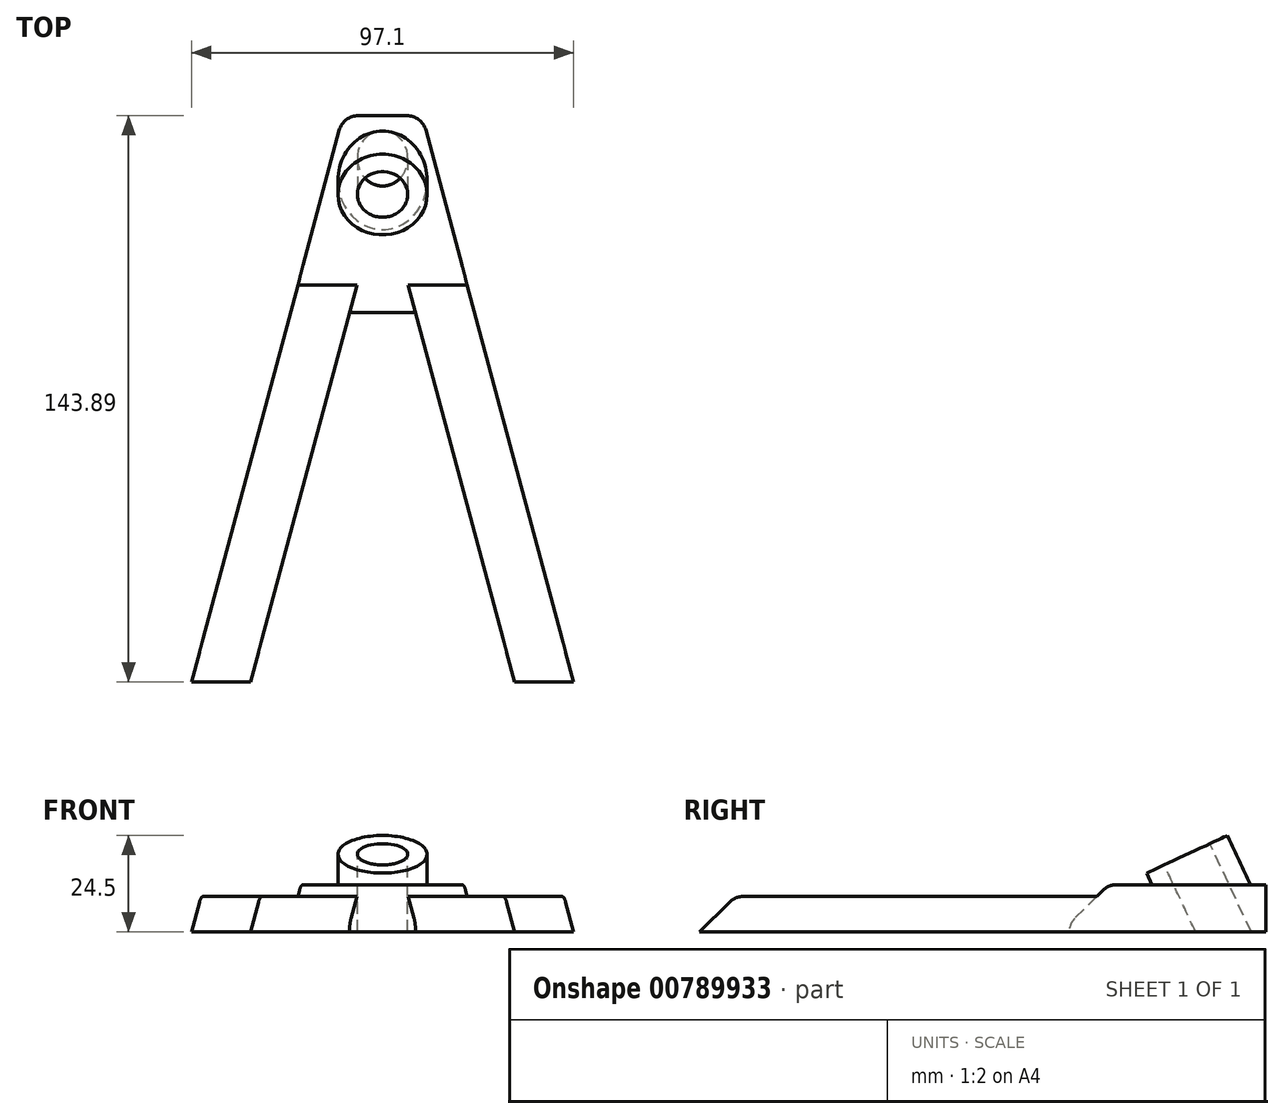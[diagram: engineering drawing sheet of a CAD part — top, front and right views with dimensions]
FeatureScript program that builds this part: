
annotation { "Feature Type Name" : "Feature", "Feature Type Description" : "" }
export const myFeature = defineFeature(function(context is Context, id is Id, definition is map)
    precondition{}
    {
        {
            var Q0;
            Q0=qCreatedBy(makeId("Top.planeOp"),FACE);
            var sketch = newSketch(context, id + "F0", { "sketchPlane" : qUnion([Q0])});
            skLineSegment(sketch, "E0", {"start": v(-48.82, -144.89) * mm, "end": v(-10, 0) * mm});
            skLineSegment(sketch, "E1", {"start": v(10, 0) * mm, "end": v(48.82, -144.89) * mm});
            skLineSegment(sketch, "E2", {"start": v(-48.82, -144.89) * mm, "end": v(-33.82, -144.89) * mm});
            skLineSegment(sketch, "E3", {"start": v(33.82, -144.89) * mm, "end": v(48.82, -144.89) * mm});
            skLineSegment(sketch, "E4", {"start": v(-33.82, -144.89) * mm, "end": v(-8.4, -50) * mm});
            skLineSegment(sketch, "E5", {"start": v(-8.4, -50) * mm, "end": v(8.4, -50) * mm});
            skLineSegment(sketch, "E6", {"start": v(8.4, -50) * mm, "end": v(33.82, -144.89) * mm});
            skPoint(sketch, "E7", {"position": v(0, 0) * mm});
            skLineSegment(sketch, "E8", {"start": v(-10, 0) * mm, "end": v(0, 0) * mm});
            skLineSegment(sketch, "E9", {"start": v(10, 0) * mm, "end": v(0, 0) * mm});
            skLineSegment(sketch, "E10", {"start": v(-8.4, -50) * mm, "end": v(-23.4, -50) * mm});
            skLineSegment(sketch, "E11", {"start": v(8.4, -50) * mm, "end": v(23.4, -50) * mm});
            skSolve(sketch);
        }
        {
            var Q0;
            {var subQ0=sQuery(id+"F0.wireOp",EDGE,"E2");Q0=makeQuery(id+"F0.imprint","IMPRINT",FACE,{"disambiguationData":[TD([[makeQuery(id+"F0.imprint","IMPRINT",EDGE,{"derivedFrom":subQ0}),1.0]])]});}
            var Q1;
            {var subQ0=sQuery(id+"F0.wireOp",EDGE,"E3");Q1=makeQuery(id+"F0.imprint","IMPRINT",FACE,{"disambiguationData":[TD([[makeQuery(id+"F0.imprint","IMPRINT",EDGE,{"derivedFrom":subQ0}),1.0]])]});}
            var Q2;
            {var subQ1=sQuery(id+"F0.wireOp",EDGE,"H4eSQYHw-7cAD-bKFQ-VINS-Qkt0nnbU60AQ");Q2=makeQuery(id+"F0.imprint","IMPRINT",FACE,{"disambiguationData":[TD([[makeQuery(id+"F0.imprint","IMPRINT",EDGE,{"derivedFrom":subQ1}),-1.0]])]});}
            var Q3;
            Q3=makeQuery(id+"F0.imprint","IMPRINT",FACE,{"disambiguationData":[TD([[makeQuery(id+"F0.imprint","IMPRINT",EDGE,{"derivedFrom":sQuery(id+"F0.wireOp",EDGE,"E5")}),1.0]])]});
            extrude(context, id + "F1", {"entities" : qUnion([Q0, Q1, Q2, Q3]), "depth" : -9 * mm, "offsetDistance" : 25 * mm});
        }
        {
            var Q0;
            Q0=qCreatedBy(makeId("Right.planeOp"),FACE);
            var sketch = newSketch(context, id + "F2", { "sketchPlane" : qUnion([Q0])});
            skLineSegment(sketch, "E12", {"start": v(-15.5, 1) * mm, "end": v(-20.03, 10.71) * mm});
            skLineSegment(sketch, "E13.0", {"start": v(-3, 1) * mm, "end": v(-9.76, 15.5) * mm});
            skLineSegment(sketch, "E14", {"start": v(-20.03, 10.71) * mm, "end": v(-9.76, 15.5) * mm});
            skLineSegment(sketch, "E15", {"start": v(-15.5, 1) * mm, "end": v(-3, 1) * mm});
            skSolve(sketch);
        }
        {
            var Q0;
            {var subQ0=sQuery(id+"F2.wireOp",EDGE,"E13.0");Q0=makeQuery(id+"F2.imprint","IMPRINT",FACE,{"disambiguationData":[TD([[makeQuery(id+"F2.imprint","IMPRINT",EDGE,{"derivedFrom":subQ0}),1.0]])]});}
            var Q1;
            Q1=sQuery(id+"F2.wireOp",EDGE,"E12");
            revolve(context, id + "F3", {"operationType" : NewBodyOperationType.ADD, "surfaceOperationType" : NewSurfaceOperationType.NEW, "entities" : qUnion([Q0]), "axis" : qUnion([Q1]), "revolveType" : RevolveType.FULL});
        }
        {
            var Q0;
            Q0=makeQuery(id+"F0.imprint","IMPRINT",FACE,{"disambiguationData":[TD([[makeQuery(id+"F0.imprint","IMPRINT",EDGE,{"derivedFrom":sQuery(id+"F0.wireOp",EDGE,"E5")}),1.0]])]});
            extrude(context, id + "F4", {"entities" : qUnion([Q0]), "operationType" : NewBodyOperationType.ADD, "depth" : 3 * mm, "offsetDistance" : 25 * mm});
        }
        {
            var Q0;
            {var subQ0=sQuery(id+"F0.wireOp",EDGE,"E8");var subQ1=sQuery(id+"F0.wireOp",EDGE,"E0");Q0=makeQuery(id+"F4.boolean.opBoolean","MERGE",EDGE,{"derivedFrom":[makeQuery(id+"F1.opExtrude","SWEPT_EDGE",EDGE,{"disambiguationData":[OSD([subQ1,subQ0])]}),makeQuery(id+"F4.opExtrude","SWEPT_EDGE",EDGE,{"disambiguationData":[OSD([subQ1,subQ0])]})]});}
            var Q1;
            {var subQ0=sQuery(id+"F0.wireOp",EDGE,"E9");var subQ1=sQuery(id+"F0.wireOp",EDGE,"E1");Q1=makeQuery(id+"F4.boolean.opBoolean","MERGE",EDGE,{"derivedFrom":[makeQuery(id+"F1.opExtrude","SWEPT_EDGE",EDGE,{"disambiguationData":[OSD([subQ1,subQ0])]}),makeQuery(id+"F4.opExtrude","SWEPT_EDGE",EDGE,{"disambiguationData":[OSD([subQ1,subQ0])]})]});}
            fillet(context, id + "F5", {"entities" : qUnion([Q0, Q1]), "radius" : 5 * mm, "tangentPropagation" : true, "allowEdgeOverflow" : false});
        }
        {
            var Q0;
            Q0=makeQuery(id+"F3.opRevolve","SWEPT_FACE",FACE,{"disambiguationData":[OSD([sQuery(id+"F2.wireOp",EDGE,"E14")])]});
            var sketch = newSketch(context, id + "F6", { "sketchPlane" : qUnion([Q0])});
            skCircle(sketch, "E16", {"center": v(0, -13.63) * mm, "radius": 6.4 * mm});
            skSolve(sketch);
        }
        {
            var Q0;
            Q0=makeQuery(id+"F6.imprint","IMPRINT",FACE,{"disambiguationData":[TD([[makeQuery(id+"F6.imprint","IMPRINT",EDGE,{"derivedFrom":sQuery(id+"F6.wireOp",EDGE,"E16")}),1.0]])]});
            extrude(context, id + "F7", {"entities" : qUnion([Q0]), "operationType" : NewBodyOperationType.REMOVE, "oppositeDirection" : true, "depth" : 30 * mm, "offsetDistance" : 25 * mm});
        }
        {
            var Q0;
            Q0=makeQuery(id+"F4.opExtrude","CAP_EDGE",EDGE,{"disambiguationData":[OSD([sQuery(id+"F0.wireOp",EDGE,"E5"),sQuery(id+"F0.wireOp",EDGE,"E10"),sQuery(id+"F0.wireOp",EDGE,"E11")])],"isStart":false});
            var Q1;
            Q1=makeQuery(id+"F1.opExtrude","CAP_EDGE",EDGE,{"disambiguationData":[OSD([sQuery(id+"F0.wireOp",EDGE,"E2")])],"isStart":true});
            var Q2;
            Q2=makeQuery(id+"F1.opExtrude","CAP_EDGE",EDGE,{"disambiguationData":[OSD([sQuery(id+"F0.wireOp",EDGE,"E3")])],"isStart":true});
            chamfer(context, id + "F8", {"entities" : qUnion([Q0, Q1, Q2]), "width" : 10 * mm, "tangentPropagation" : true});
        }
        {
            var Q0;
            {var subQ0=sQuery(id+"F0.wireOp",EDGE,"E11");var subQ1=sQuery(id+"F0.wireOp",EDGE,"E10");var subQ2=sQuery(id+"F0.wireOp",EDGE,"E5");Q0=makeQuery(id+"F8.opChamfer","BLEND_EDGE",EDGE,{"blendedFrom":[makeQuery(id+"F4.opExtrude","CAP_EDGE",EDGE,{"disambiguationData":[OSD([subQ2,subQ1,subQ0])],"isStart":false}),makeQuery(id+"F4.opExtrude","CAP_FACE",FACE,{"disambiguationData":[OSD([sQuery(id+"F0.wireOp",EDGE,"E0"),sQuery(id+"F0.wireOp",EDGE,"E1"),subQ2,sQuery(id+"F0.wireOp",EDGE,"E8"),sQuery(id+"F0.wireOp",EDGE,"E9"),subQ1,subQ0])],"isStart":false})],"blendedInto":[makeQuery(id+"F4.opExtrude","CAP_FACE",FACE,{"disambiguationData":[OSD([sQuery(id+"F0.wireOp",EDGE,"E0"),sQuery(id+"F0.wireOp",EDGE,"E1"),subQ2,sQuery(id+"F0.wireOp",EDGE,"E8"),sQuery(id+"F0.wireOp",EDGE,"E9"),subQ1,subQ0])],"isStart":false})]});}
            var Q1;
            {var subQ0=sQuery(id+"F0.wireOp",EDGE,"E5");var subQ1=sQuery(id+"F0.wireOp",EDGE,"E4");var subQ2=sQuery(id+"F0.wireOp",EDGE,"E2");var subQ3=sQuery(id+"F0.wireOp",EDGE,"E0");Q1=makeQuery(id+"F8.opChamfer","BLEND_EDGE",EDGE,{"blendedFrom":[makeQuery(id+"F1.opExtrude","CAP_EDGE",EDGE,{"disambiguationData":[OSD([subQ2])],"isStart":true}),makeQuery(id+"F4.boolean.opBoolean","SPLIT",FACE,{"disambiguationData":[TD([makeQuery(id+"F1.opExtrude","SWEPT_FACE",FACE,{"disambiguationData":[OSD([subQ3])]})])],"derivedFrom":makeQuery(id+"F1.opExtrude","CAP_FACE",FACE,{"disambiguationData":[OSD([subQ3,sQuery(id+"F0.wireOp",EDGE,"E1"),subQ2,sQuery(id+"F0.wireOp",EDGE,"E3"),subQ1,subQ0,sQuery(id+"F0.wireOp",EDGE,"E6"),sQuery(id+"F0.wireOp",EDGE,"E8"),sQuery(id+"F0.wireOp",EDGE,"E9")])],"isStart":true})})],"blendedInto":[makeQuery(id+"F4.boolean.opBoolean","SPLIT",FACE,{"disambiguationData":[TD([makeQuery(id+"F1.opExtrude","SWEPT_FACE",FACE,{"disambiguationData":[OSD([subQ3])]})])],"derivedFrom":makeQuery(id+"F1.opExtrude","CAP_FACE",FACE,{"disambiguationData":[OSD([subQ3,sQuery(id+"F0.wireOp",EDGE,"E1"),subQ2,sQuery(id+"F0.wireOp",EDGE,"E3"),subQ1,subQ0,sQuery(id+"F0.wireOp",EDGE,"E6"),sQuery(id+"F0.wireOp",EDGE,"E8"),sQuery(id+"F0.wireOp",EDGE,"E9")])],"isStart":true})})]});}
            var Q2;
            {var subQ0=sQuery(id+"F0.wireOp",EDGE,"E5");var subQ1=sQuery(id+"F0.wireOp",EDGE,"E3");var subQ2=sQuery(id+"F0.wireOp",EDGE,"E6");var subQ3=sQuery(id+"F0.wireOp",EDGE,"E1");Q2=makeQuery(id+"F8.opChamfer","BLEND_EDGE",EDGE,{"blendedFrom":[makeQuery(id+"F1.opExtrude","CAP_EDGE",EDGE,{"disambiguationData":[OSD([subQ1])],"isStart":true}),makeQuery(id+"F4.boolean.opBoolean","SPLIT",FACE,{"disambiguationData":[TD([makeQuery(id+"F1.opExtrude","SWEPT_FACE",FACE,{"disambiguationData":[OSD([subQ3])]})])],"derivedFrom":makeQuery(id+"F1.opExtrude","CAP_FACE",FACE,{"disambiguationData":[OSD([sQuery(id+"F0.wireOp",EDGE,"E0"),subQ3,sQuery(id+"F0.wireOp",EDGE,"E2"),subQ1,sQuery(id+"F0.wireOp",EDGE,"E4"),subQ0,subQ2,sQuery(id+"F0.wireOp",EDGE,"E8"),sQuery(id+"F0.wireOp",EDGE,"E9")])],"isStart":true})})],"blendedInto":[makeQuery(id+"F4.boolean.opBoolean","SPLIT",FACE,{"disambiguationData":[TD([makeQuery(id+"F1.opExtrude","SWEPT_FACE",FACE,{"disambiguationData":[OSD([subQ3])]})])],"derivedFrom":makeQuery(id+"F1.opExtrude","CAP_FACE",FACE,{"disambiguationData":[OSD([sQuery(id+"F0.wireOp",EDGE,"E0"),subQ3,sQuery(id+"F0.wireOp",EDGE,"E2"),subQ1,sQuery(id+"F0.wireOp",EDGE,"E4"),subQ0,subQ2,sQuery(id+"F0.wireOp",EDGE,"E8"),sQuery(id+"F0.wireOp",EDGE,"E9")])],"isStart":true})})]});}
            var Q3;
            {var subQ0=sQuery(id+"F0.wireOp",EDGE,"E11");var subQ1=sQuery(id+"F0.wireOp",EDGE,"E10");var subQ2=sQuery(id+"F0.wireOp",EDGE,"E5");Q3=makeQuery(id+"F8.opChamfer","BLEND_EDGE",EDGE,{"blendedFrom":[makeQuery(id+"F4.opExtrude","CAP_EDGE",EDGE,{"disambiguationData":[OSD([subQ2,subQ1,subQ0])],"isStart":false}),makeQuery(id+"F4.boolean.opBoolean","MERGE",FACE,{"derivedFrom":[makeQuery(id+"F1.opExtrude","SWEPT_FACE",FACE,{"disambiguationData":[OSD([subQ2])]}),makeQuery(id+"F4.opExtrude","SWEPT_FACE",FACE,{"disambiguationData":[OSD([subQ2,subQ1,subQ0])]})]})],"blendedInto":[makeQuery(id+"F4.boolean.opBoolean","MERGE",FACE,{"derivedFrom":[makeQuery(id+"F1.opExtrude","SWEPT_FACE",FACE,{"disambiguationData":[OSD([subQ2])]}),makeQuery(id+"F4.opExtrude","SWEPT_FACE",FACE,{"disambiguationData":[OSD([subQ2,subQ1,subQ0])]})]})]});}
            fillet(context, id + "F9", {"entities" : qUnion([Q0, Q1, Q2, Q3]), "radius" : 5 * mm, "tangentPropagation" : true, "allowEdgeOverflow" : false});
        }
    });
